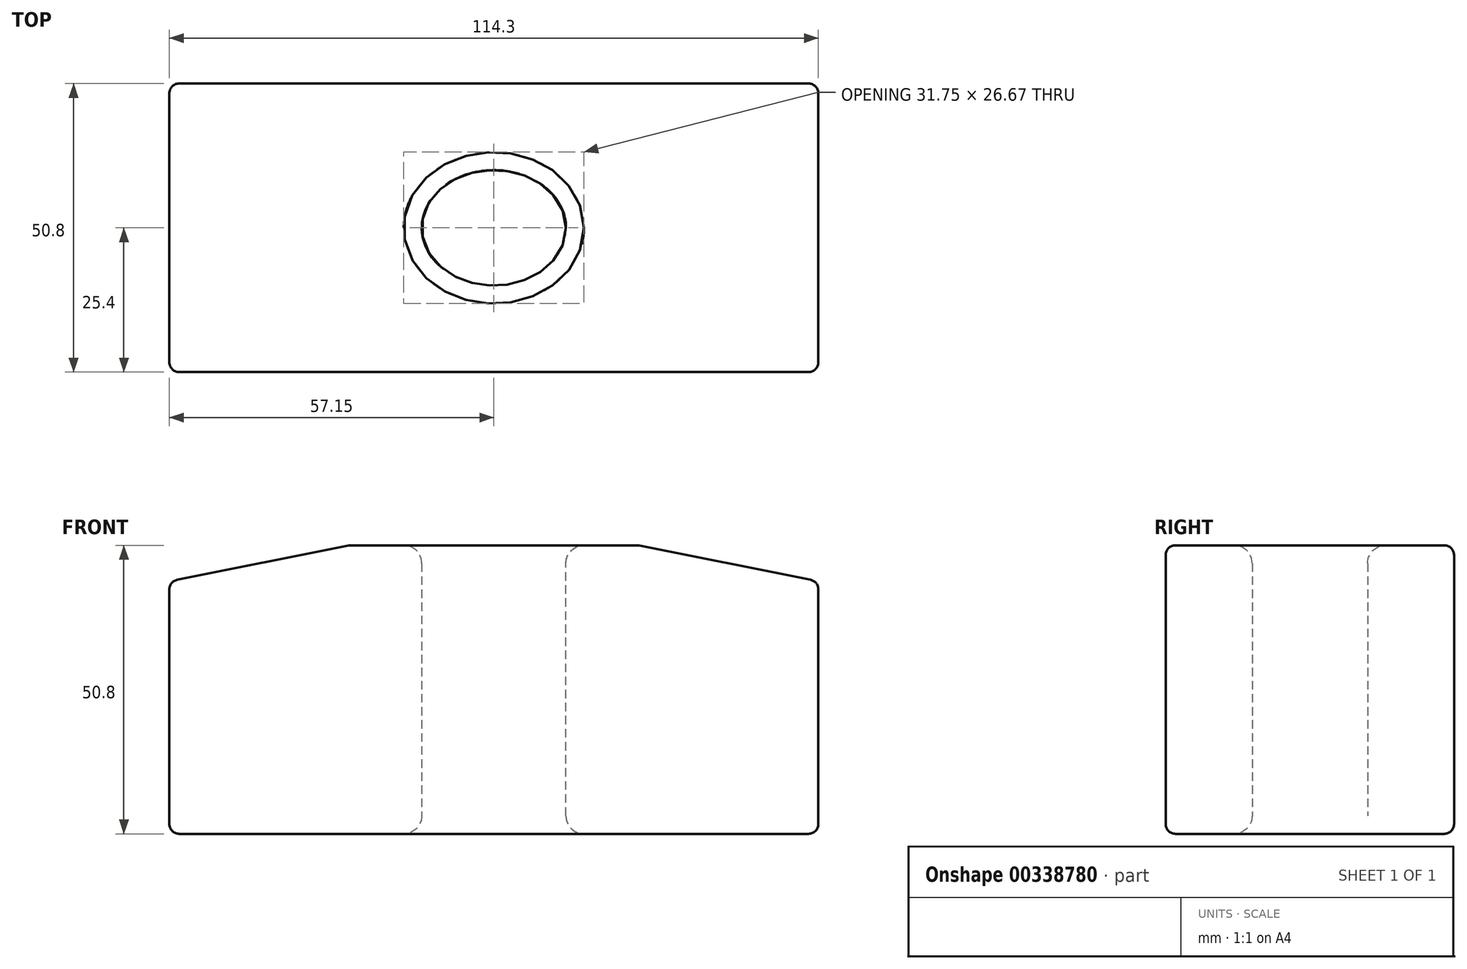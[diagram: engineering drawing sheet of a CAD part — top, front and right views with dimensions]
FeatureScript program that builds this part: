
annotation { "Feature Type Name" : "Feature", "Feature Type Description" : "" }
export const myFeature = defineFeature(function(context is Context, id is Id, definition is map)
    precondition{}
    {
        {
            var Q0;
            Q0=qCreatedBy(makeId("Front.planeOp"),FACE);
            var sketch = newSketch(context, id + "F0", { "sketchPlane" : qUnion([Q0])});
            skLineSegment(sketch, "E0.bottom", {"start": v(0, 0) * mm, "end": v(114.3, 0) * mm});
            skLineSegment(sketch, "E0.top", {"start": v(0, 50.8) * mm, "end": v(114.3, 50.8) * mm});
            skLineSegment(sketch, "E0.left", {"start": v(0, 0) * mm, "end": v(0, 50.8) * mm});
            skLineSegment(sketch, "E0.right", {"start": v(114.3, 0) * mm, "end": v(114.3, 50.8) * mm});
            skSolve(sketch);
        }
        {
            var Q0;
            Q0=makeQuery(id+"F0.imprint","IMPRINT",FACE,{"disambiguationData":[TD([[makeQuery(id+"F0.imprint","IMPRINT",EDGE,{"derivedFrom":sQuery(id+"F0.wireOp",EDGE,"E0.bottom")}),1.0]])]});
            extrude(context, id + "F1", {"entities" : qUnion([Q0]), "depth" : 50.8 * mm});
        }
        {
            var Q0;
            Q0=makeQuery(id+"F1.opExtrude","SWEPT_FACE",FACE,{"disambiguationData":[OSD([sQuery(id+"F0.wireOp",EDGE,"E0.top")])]});
            var sketch = newSketch(context, id + "F2", { "sketchPlane" : qUnion([Q0])});
            skEllipse(sketch, "E1", {"center": v(57.15, -25.4) * mm, "majorRadius": 12.7 * mm, "minorRadius": 10.16 * mm, "majorAxis": v(1, 0)});
            skPoint(sketch, "E1.centerSnap0", {"position": v(57.15, -50.8) * mm});
            skPoint(sketch, "E1.centerSnap1", {"position": v(114.3, -25.4) * mm});
            skSolve(sketch);
        }
        {
            var Q0;
            Q0=makeQuery(id+"F2.imprint","IMPRINT",FACE,{"disambiguationData":[TD([[makeQuery(id+"F2.imprint","IMPRINT",EDGE,{"derivedFrom":sQuery(id+"F2.wireOp",EDGE,"E1")}),1.0]])]});
            extrude(context, id + "F3", {"entities" : qUnion([Q0]), "operationType" : NewBodyOperationType.REMOVE, "endBound" : BoundingType.THROUGH_ALL, "oppositeDirection" : true, "depth" : 25.4 * mm});
        }
        {
            var Q0;
            Q0=makeQuery(id+"F3.boolean.opBoolean","COPY",FACE,{"derivedFrom":makeQuery(id+"F3.opExtrude","SWEPT_FACE",FACE,{"disambiguationData":[OSD([sQuery(id+"F2.wireOp",EDGE,"E1")])]})});
            fillet(context, id + "F4", {"entities" : qUnion([Q0]), "radius" : 3.17 * mm, "tangentPropagation" : true, "allowEdgeOverflow" : false});
        }
        {
            var Q0;
            Q0=makeQuery(id+"F1.opExtrude","CAP_FACE",FACE,{"disambiguationData":[OSD([sQuery(id+"F0.wireOp",EDGE,"E0.bottom"),sQuery(id+"F0.wireOp",EDGE,"E0.top"),sQuery(id+"F0.wireOp",EDGE,"E0.left"),sQuery(id+"F0.wireOp",EDGE,"E0.right")])],"isStart":false});
            var sketch = newSketch(context, id + "F5", { "sketchPlane" : qUnion([Q0])});
            skLineSegment(sketch, "E2", {"start": v(31.75, 50.8) * mm, "end": v(0, 44.45) * mm});
            skLineSegment(sketch, "E3", {"start": v(0, 44.45) * mm, "end": v(0, 57.15) * mm});
            skLineSegment(sketch, "E4", {"start": v(0, 57.15) * mm, "end": v(114.3, 57.15) * mm});
            skLineSegment(sketch, "E5", {"start": v(114.3, 57.15) * mm, "end": v(114.3, 44.45) * mm});
            skLineSegment(sketch, "E6", {"start": v(114.3, 44.45) * mm, "end": v(82.55, 50.8) * mm});
            skLineSegment(sketch, "E7", {"start": v(82.55, 50.8) * mm, "end": v(31.75, 50.8) * mm});
            skSolve(sketch);
        }
        {
            var Q0;
            Q0 = qSketchRegion(id + "F5", true);
            extrude(context, id + "F6", {"entities" : qUnion([Q0]), "operationType" : NewBodyOperationType.REMOVE, "endBound" : BoundingType.THROUGH_ALL, "oppositeDirection" : true, "depth" : 25.4 * mm});
        }
        {
            var Q0;
            Q0=makeQuery(id+"F6.boolean.opBoolean","COPY",FACE,{"derivedFrom":makeQuery(id+"F6.opExtrude","SWEPT_FACE",FACE,{"disambiguationData":[OSD([sQuery(id+"F5.wireOp",EDGE,"E2")])]})});
            var Q1;
            Q1=makeQuery(id+"F1.opExtrude","SWEPT_FACE",FACE,{"disambiguationData":[OSD([sQuery(id+"F0.wireOp",EDGE,"E0.top")])]});
            var Q2;
            Q2=makeQuery(id+"F6.boolean.opBoolean","COPY",FACE,{"derivedFrom":makeQuery(id+"F6.opExtrude","SWEPT_FACE",FACE,{"disambiguationData":[OSD([sQuery(id+"F5.wireOp",EDGE,"E6")])]})});
            var Q3;
            Q3=makeQuery(id+"F1.opExtrude","CAP_FACE",FACE,{"disambiguationData":[OSD([sQuery(id+"F0.wireOp",EDGE,"E0.bottom"),sQuery(id+"F0.wireOp",EDGE,"E0.top"),sQuery(id+"F0.wireOp",EDGE,"E0.left"),sQuery(id+"F0.wireOp",EDGE,"E0.right")])],"isStart":false});
            var Q4;
            Q4=makeQuery(id+"F1.opExtrude","SWEPT_FACE",FACE,{"disambiguationData":[OSD([sQuery(id+"F0.wireOp",EDGE,"E0.right")])]});
            var Q5;
            Q5=makeQuery(id+"F1.opExtrude","CAP_FACE",FACE,{"disambiguationData":[OSD([sQuery(id+"F0.wireOp",EDGE,"E0.bottom"),sQuery(id+"F0.wireOp",EDGE,"E0.top"),sQuery(id+"F0.wireOp",EDGE,"E0.left"),sQuery(id+"F0.wireOp",EDGE,"E0.right")])],"isStart":true});
            var Q6;
            Q6=makeQuery(id+"F1.opExtrude","SWEPT_FACE",FACE,{"disambiguationData":[OSD([sQuery(id+"F0.wireOp",EDGE,"E0.bottom")])]});
            fillet(context, id + "F7", {"entities" : qUnion([Q0, Q1, Q2, Q3, Q4, Q5, Q6]), "radius" : 1.71 * mm, "tangentPropagation" : true, "allowEdgeOverflow" : false});
        }
    });
